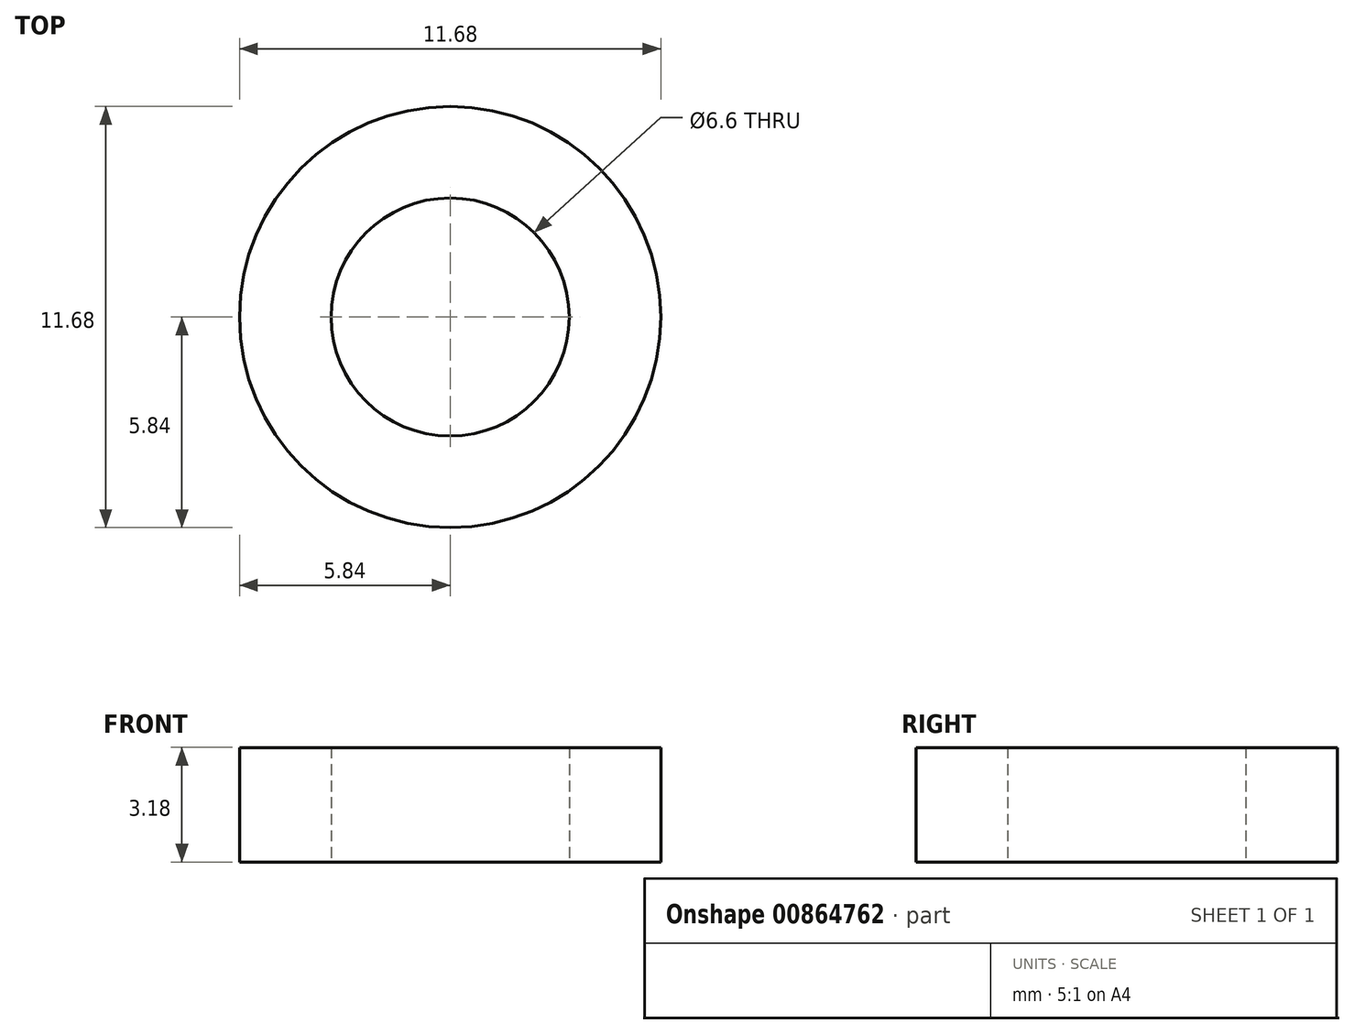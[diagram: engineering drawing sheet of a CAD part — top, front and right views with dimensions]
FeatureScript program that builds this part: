
annotation { "Feature Type Name" : "Feature", "Feature Type Description" : "" }
export const myFeature = defineFeature(function(context is Context, id is Id, definition is map)
    precondition{}
    {
        {
            var Q0;
            Q0=qCreatedBy(makeId("Top.planeOp"),FACE);
            var sketch = newSketch(context, id + "F0", { "sketchPlane" : qUnion([Q0])});
            skCircle(sketch, "E0", {"center": v(0, 0) * mm, "radius": 3.3 * mm});
            skCircle(sketch, "E1", {"center": v(0, 0) * mm, "radius": 5.84 * mm});
            skSolve(sketch);
        }
        {
            var Q0;
            Q0=makeQuery(id+"F0.imprint","IMPRINT",FACE,{"disambiguationData":[TD([[makeQuery(id+"F0.imprint","IMPRINT",EDGE,{"derivedFrom":sQuery(id+"F0.wireOp",EDGE,"E0")}),-1.0]])]});
            extrude(context, id + "F1", {"entities" : qUnion([Q0]), "depth" : 3.17 * mm, "offsetDistance" : 25.4 * mm});
        }
    });
